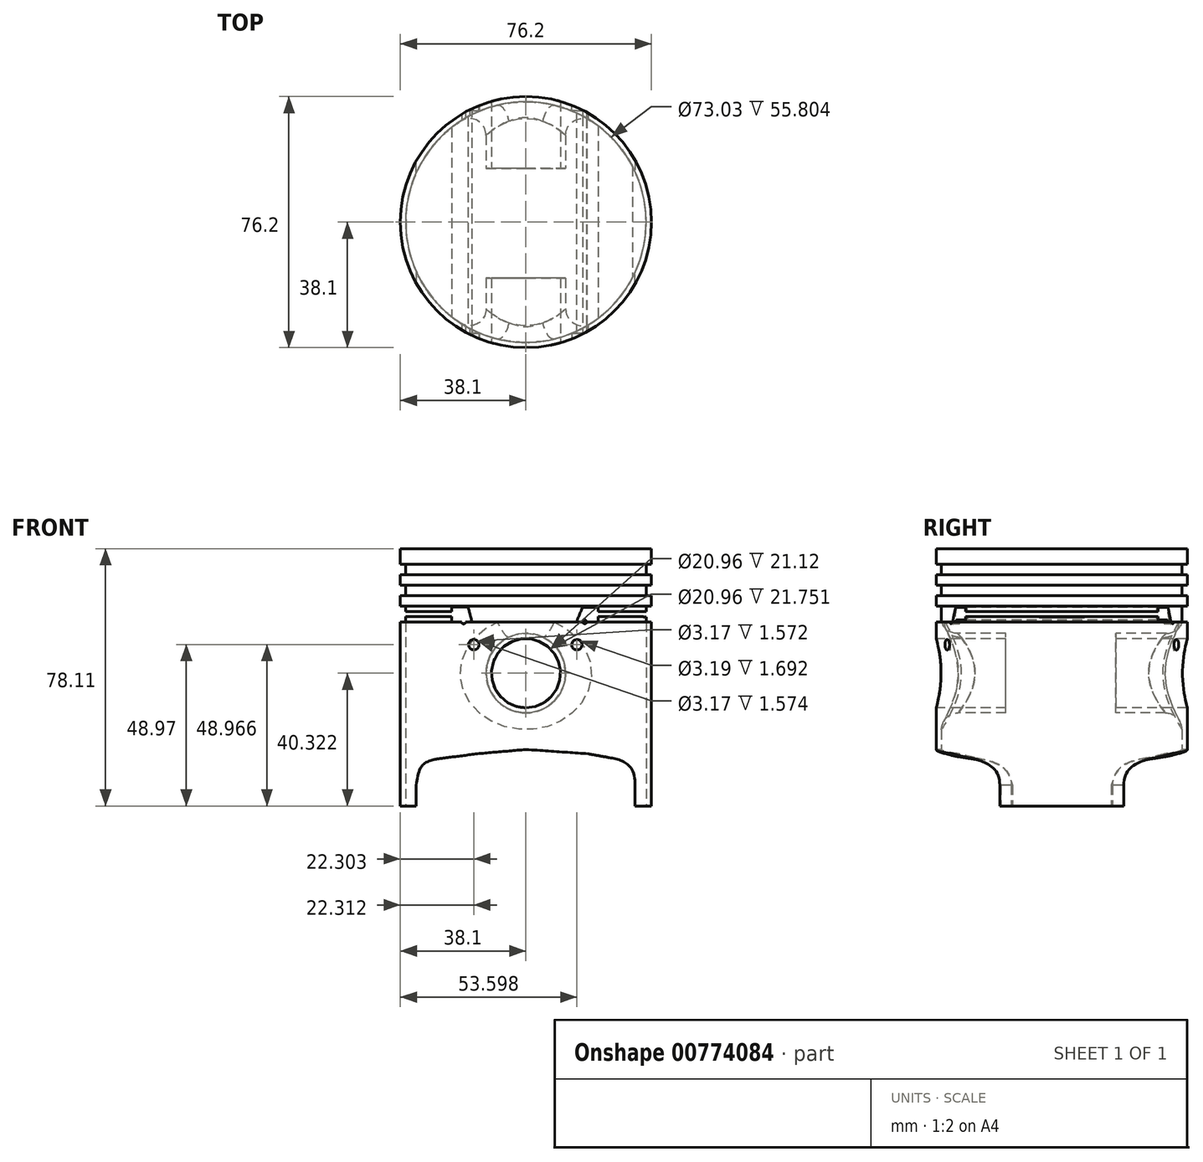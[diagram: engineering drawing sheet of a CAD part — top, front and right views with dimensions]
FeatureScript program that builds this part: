
annotation { "Feature Type Name" : "Feature", "Feature Type Description" : "" }
export const myFeature = defineFeature(function(context is Context, id is Id, definition is map)
    precondition{}
    {
        {
            var Q0;
            Q0=qCreatedBy(makeId("Top.planeOp"),FACE);
            var sketch = newSketch(context, id + "F0", { "sketchPlane" : qUnion([Q0])});
            skCircle(sketch, "E0", {"center": v(0, 0) * mm, "radius": 38.1 * mm});
            skSolve(sketch);
        }
        {
            var Q0;
            Q0=makeQuery(id+"F0.imprint","IMPRINT",FACE,{"disambiguationData":[TD([[makeQuery(id+"F0.imprint","IMPRINT",EDGE,{"derivedFrom":sQuery(id+"F0.wireOp",EDGE,"E0")}),1.0]])]});
            extrude(context, id + "F1", {"entities" : qUnion([Q0]), "depth" : 76.2 * mm, "offsetDistance" : 25.4 * mm});
        }
        {
            var Q0;
            Q0=qCreatedBy(makeId("Front.planeOp"),FACE);
            var sketch = newSketch(context, id + "F2", { "sketchPlane" : qUnion([Q0])});
            skCircle(sketch, "E1", {"center": v(0, 40.32) * mm, "radius": 10.48 * mm});
            skLineSegment(sketch, "E2", {"start": v(-33.3, 0) * mm, "end": v(-33.3, 6.35) * mm});
            skFitSpline(sketch, "E3", {"points": [v(-33.3, 6.35) * mm, v(-31.23, 12.52) * mm, v(-25.36, 14.53) * mm, v(-14.25, 15.88) * mm], "startDerivative": vector(3.82, 23.7) * mm, "endDerivative": vector(29.34, 3.33) * mm});
            skLineSegment(sketch, "E4", {"start": v(0.15, 29.85) * mm, "end": v(0.09, 17.15) * mm});
            skLineSegment(sketch, "E5", {"start": v(-14.25, 15.88) * mm, "end": v(0.09, 17.15) * mm});
            skLineSegment(sketch, "E6", {"start": v(33.13, 0) * mm, "end": v(33.13, 6.35) * mm});
            skLineSegment(sketch, "E7", {"start": v(0.09, 17.15) * mm, "end": v(18.85, 15.87) * mm});
            skPoint(sketch, "E8.2.internal.snap0", {"position": v(25.18, 5.16) * mm});
            skFitSpline(sketch, "E8", {"points": [v(18.85, 15.88) * mm, v(25.18, 14.52) * mm, v(25.18, 14.55) * mm], "startDerivative": vector(9.4, -2.2) * mm, "endDerivative": vector(-0.36, 0.95) * mm});
            skFitSpline(sketch, "E9", {"points": [v(25.18, 14.53) * mm, v(31.08, 12.52) * mm, v(33.13, 6.35) * mm], "startDerivative": vector(17.9, -3.2) * mm, "endDerivative": vector(-0.8, -16.63) * mm});
            skLineSegment(sketch, "E10", {"start": v(33.13, 0) * mm, "end": v(33.13, -4.57) * mm});
            skLineSegment(sketch, "E11", {"start": v(-33.3, 0) * mm, "end": v(-33.3, -6.09) * mm});
            skSolve(sketch);
        }
        {
            var Q0;
            Q0 = qSketchRegion(id + "F2", true);
            extrude(context, id + "F3", {"entities" : qUnion([Q0]), "operationType" : NewBodyOperationType.REMOVE, "oppositeDirection" : true, "depth" : 101.6 * mm, "offsetDistance" : 25.4 * mm, "hasSecondDirection" : true, "secondDirectionOppositeDirection" : false, "secondDirectionDepth" : 101.6 * mm});
        }
        {
            var Q0;
            Q0=qCreatedBy(makeId("Front.planeOp"),FACE);
            var sketch = newSketch(context, id + "F4", { "sketchPlane" : qUnion([Q0])});
            skLineSegment(sketch, "E12", {"start": v(33.14, -4.56) * mm, "end": v(33.14, 6.35) * mm});
            skFitSpline(sketch, "E13", {"points": [v(33.14, 6.35) * mm, v(32.85, 9.25) * mm, v(31.86, 11.6) * mm, v(30.17, 13.16) * mm, v(27.81, 14.2) * mm, v(25.2, 14.7) * mm, v(25.16, 14.64) * mm], "startDerivative": vector(-0.6, 14.42) * mm, "endDerivative": vector(43.72, -13.84) * mm});
            skLineSegment(sketch, "E14", {"start": v(0, 17.15) * mm, "end": v(18.85, 15.85) * mm});
            skLineSegment(sketch, "E15", {"start": v(18.85, 15.85) * mm, "end": v(25.2, 14.7) * mm});
            skLineSegment(sketch, "E16", {"start": v(-33.3, -6.02) * mm, "end": v(-33.3, 6.35) * mm});
            skFitSpline(sketch, "E17", {"points": [v(-33.3, 6.35) * mm, v(-32.71, 9.52) * mm, v(-31.31, 12.43) * mm, v(-28.65, 13.9) * mm, v(-25.45, 14.48) * mm], "startDerivative": vector(1.77, 12.54) * mm, "endDerivative": vector(12.84, 1.63) * mm});
            skLineSegment(sketch, "E18", {"start": v(-25.45, 14.48) * mm, "end": v(-14.19, 15.92) * mm});
            skLineSegment(sketch, "E19", {"start": v(-14.19, 15.92) * mm, "end": v(0, 17.15) * mm});
            skLineSegment(sketch, "E20", {"start": v(33.14, -4.56) * mm, "end": v(-33.3, -6.02) * mm});
            skSolve(sketch);
        }
        {
            var Q0;
            {var subQ2=sQuery(id+"F4.wireOp",EDGE,"E12");Q0=makeQuery(id+"F4.imprint","IMPRINT",FACE,{"disambiguationData":[TD([[makeQuery(id+"F4.imprint","IMPRINT",EDGE,{"derivedFrom":subQ2}),1.0]])]});}
            extrude(context, id + "F5", {"entities" : qUnion([Q0]), "operationType" : NewBodyOperationType.REMOVE, "oppositeDirection" : true, "depth" : 50.8 * mm, "offsetDistance" : 25.4 * mm, "hasSecondDirection" : true, "secondDirectionOppositeDirection" : false, "secondDirectionDepth" : 50.8 * mm});
        }
        {
            var Q0;
            Q0=makeQuery(id+"F5.boolean.opBoolean","COPY",FACE,{"derivedFrom":makeQuery(id+"F5.opExtrude","SWEPT_FACE",FACE,{"disambiguationData":[OSD([sQuery(id+"F4.wireOp",EDGE,"E19")])]})});
            var Q1;
            Q1=makeQuery(id+"F5.boolean.opBoolean","COPY",FACE,{"derivedFrom":makeQuery(id+"F5.opExtrude","SWEPT_FACE",FACE,{"disambiguationData":[OSD([sQuery(id+"F4.wireOp",EDGE,"E18")])]})});
            var Q2;
            Q2=makeQuery(id+"F5.boolean.opBoolean","COPY",FACE,{"derivedFrom":makeQuery(id+"F5.opExtrude","SWEPT_FACE",FACE,{"disambiguationData":[OSD([sQuery(id+"F4.wireOp",EDGE,"E17")])]})});
            var Q3;
            Q3=makeQuery(id+"F5.boolean.opBoolean","COPY",FACE,{"derivedFrom":makeQuery(id+"F5.opExtrude","SWEPT_FACE",FACE,{"disambiguationData":[OSD([sQuery(id+"F4.wireOp",EDGE,"E14")])]})});
            var Q4;
            Q4=makeQuery(id+"F5.boolean.opBoolean","COPY",FACE,{"derivedFrom":makeQuery(id+"F5.opExtrude","SWEPT_FACE",FACE,{"disambiguationData":[OSD([sQuery(id+"F4.wireOp",EDGE,"E15")])]})});
            var Q5;
            Q5=makeQuery(id+"F5.boolean.opBoolean","COPY",FACE,{"derivedFrom":makeQuery(id+"F5.opExtrude","SWEPT_FACE",FACE,{"disambiguationData":[OSD([sQuery(id+"F4.wireOp",EDGE,"E13")])]})});
            var Q6;
            {var subQ0=sQuery(id+"F0.wireOp",EDGE,"E0");Q6=makeQuery(id+"F5.boolean.opBoolean","SPLIT",FACE,{"disambiguationData":[TD([makeQuery(id+"F5.opExtrude","SWEPT_FACE",FACE,{"disambiguationData":[OSD([sQuery(id+"F4.wireOp",EDGE,"E12")])]})])],"derivedFrom":makeQuery(id+"F1.opExtrude","CAP_FACE",FACE,{"disambiguationData":[OSD([subQ0])],"isStart":true})});}
            var Q7;
            {var subQ0=sQuery(id+"F0.wireOp",EDGE,"E0");Q7=makeQuery(id+"F5.boolean.opBoolean","SPLIT",FACE,{"disambiguationData":[TD([makeQuery(id+"F5.opExtrude","SWEPT_FACE",FACE,{"disambiguationData":[OSD([sQuery(id+"F4.wireOp",EDGE,"E16")])]})])],"derivedFrom":makeQuery(id+"F1.opExtrude","CAP_FACE",FACE,{"disambiguationData":[OSD([subQ0])],"isStart":true})});}
            var Q8;
            Q8=makeQuery(id+"F5.boolean.opBoolean","COPY",FACE,{"derivedFrom":makeQuery(id+"F5.opExtrude","SWEPT_FACE",FACE,{"disambiguationData":[OSD([sQuery(id+"F4.wireOp",EDGE,"E16")])]})});
            var Q9;
            Q9=makeQuery(id+"F5.boolean.opBoolean","COPY",FACE,{"derivedFrom":makeQuery(id+"F5.opExtrude","SWEPT_FACE",FACE,{"disambiguationData":[OSD([sQuery(id+"F4.wireOp",EDGE,"E12")])]})});
            shell(context, id + "F6", {"entities" : qUnion([Q0, Q1, Q2, Q3, Q4, Q5, Q6, Q7, Q8, Q9]), "thickness" : 1.59 * mm});
        }
        {
            var Q0;
            Q0=qCreatedBy(makeId("Top.planeOp"),FACE);
            var sketch = newSketch(context, id + "F7", { "sketchPlane" : qUnion([Q0])});
            skLineSegment(sketch, "E21", {"start": v(-14.71, -16.98) * mm, "end": v(14.08, -16.98) * mm});
            skLineSegment(sketch, "E22", {"start": v(14.08, -16.98) * mm, "end": v(14.08, 16.35) * mm});
            skLineSegment(sketch, "E23", {"start": v(14.08, 16.35) * mm, "end": v(-13.8, 16.35) * mm});
            skLineSegment(sketch, "E24", {"start": v(-14.71, -16.98) * mm, "end": v(-13.8, 16.35) * mm});
            skLineSegment(sketch, "E25", {"start": v(0, -37.71) * mm, "end": v(-4.68, -37.71) * mm});
            skLineSegment(sketch, "E26", {"start": v(0, 37.07) * mm, "end": v(2.12, 37.07) * mm});
            skSolve(sketch);
        }
        {
            var Q0;
            Q0=makeQuery(id+"F7.imprint","IMPRINT",FACE,{"disambiguationData":[TD([[makeQuery(id+"F7.imprint","IMPRINT",EDGE,{"derivedFrom":sQuery(id+"F7.wireOp",EDGE,"E21")}),1.0]])]});
            extrude(context, id + "F8", {"entities" : qUnion([Q0]), "operationType" : NewBodyOperationType.REMOVE, "oppositeDirection" : true, "depth" : 25.4 * mm, "offsetDistance" : 25.4 * mm, "hasSecondDirection" : true, "secondDirectionOppositeDirection" : false, "secondDirectionDepth" : 55.88 * mm});
        }
        {
            var Q0;
            Q0=qCreatedBy(makeId("Front.planeOp"),FACE);
            var sketch = newSketch(context, id + "F9", { "sketchPlane" : qUnion([Q0])});
            skLineSegment(sketch, "E27", {"start": v(-50.34, 76.44) * mm, "end": v(-50.34, 55.8) * mm});
            skLineSegment(sketch, "E28", {"start": v(-50.34, 76.44) * mm, "end": v(56.34, 76.44) * mm});
            skLineSegment(sketch, "E29", {"start": v(56.34, 76.44) * mm, "end": v(56.34, 55.8) * mm});
            skLineSegment(sketch, "E30", {"start": v(56.34, 55.8) * mm, "end": v(-50.34, 55.8) * mm});
            skSolve(sketch);
        }
        {
            var Q0;
            Q0=makeQuery(id+"F9.imprint","IMPRINT",FACE,{"disambiguationData":[TD([[makeQuery(id+"F9.imprint","IMPRINT",EDGE,{"derivedFrom":sQuery(id+"F9.wireOp",EDGE,"E27")}),1.0]])]});
            extrude(context, id + "F10", {"entities" : qUnion([Q0]), "operationType" : NewBodyOperationType.REMOVE, "oppositeDirection" : true, "depth" : 81.28 * mm, "offsetDistance" : 25.4 * mm, "hasSecondDirection" : true, "secondDirectionOppositeDirection" : false, "secondDirectionDepth" : 50.8 * mm});
        }
        {
            var Q0;
            Q0=qCreatedBy(makeId("Top.planeOp"),FACE);
            cPlane(context, id + "F11", {"entities" : qUnion([Q0]), "cplaneType" : CPlaneType.OFFSET, "offset" : 55.88 * mm, "width" : 152.4 * mm, "height" : 152.4 * mm});
        }
        {
            var Q0;
            Q0=qCreatedBy(id+"F11.planeOp",FACE);
            var sketch = newSketch(context, id + "F12", { "sketchPlane" : qUnion([Q0])});
            skCircle(sketch, "E31", {"center": v(0, 0) * mm, "radius": 36.51 * mm});
            skSolve(sketch);
        }
        {
            var Q0;
            Q0 = qSketchRegion(id + "F12", true);
            extrude(context, id + "F13", {"entities" : qUnion([Q0]), "depth" : 4.76 * mm, "offsetDistance" : 25.4 * mm});
        }
        {
            var Q0;
            Q0=qCreatedBy(id+"F11.planeOp",FACE);
            cPlane(context, id + "F14", {"entities" : qUnion([Q0]), "cplaneType" : CPlaneType.OFFSET, "offset" : 4.76 * mm, "width" : 152.4 * mm, "height" : 152.4 * mm});
        }
        {
            var Q0;
            Q0=qCreatedBy(id+"F14.planeOp",FACE);
            var sketch = newSketch(context, id + "F15", { "sketchPlane" : qUnion([Q0])});
            skCircle(sketch, "E32", {"center": v(0, 0) * mm, "radius": 38.1 * mm});
            skSolve(sketch);
        }
        {
            var Q0;
            Q0 = qSketchRegion(id + "F15", true);
            extrude(context, id + "F16", {"entities" : qUnion([Q0]), "operationType" : NewBodyOperationType.ADD, "depth" : 3.17 * mm, "offsetDistance" : 25.4 * mm});
        }
        {
            var Q0;
            Q0=qCreatedBy(id+"F14.planeOp",FACE);
            cPlane(context, id + "F17", {"entities" : qUnion([Q0]), "cplaneType" : CPlaneType.OFFSET, "offset" : 3.17 * mm, "width" : 152.4 * mm, "height" : 152.4 * mm});
        }
        {
            var Q0;
            Q0=qCreatedBy(id+"F17.planeOp",FACE);
            var sketch = newSketch(context, id + "F18", { "sketchPlane" : qUnion([Q0])});
            skCircle(sketch, "E33", {"center": v(0, 0) * mm, "radius": 36.51 * mm});
            skSolve(sketch);
        }
        {
            var Q0;
            Q0 = qSketchRegion(id + "F18", true);
            extrude(context, id + "F19", {"entities" : qUnion([Q0]), "operationType" : NewBodyOperationType.ADD, "depth" : 3.17 * mm, "offsetDistance" : 25.4 * mm});
        }
        {
            var Q0;
            Q0=qCreatedBy(id+"F17.planeOp",FACE);
            cPlane(context, id + "F20", {"entities" : qUnion([Q0]), "cplaneType" : CPlaneType.OFFSET, "offset" : 3.17 * mm, "width" : 152.4 * mm, "height" : 152.4 * mm});
        }
        {
            var Q0;
            Q0=qCreatedBy(id+"F20.planeOp",FACE);
            var sketch = newSketch(context, id + "F21", { "sketchPlane" : qUnion([Q0])});
            skCircle(sketch, "E34", {"center": v(0, 0) * mm, "radius": 38.1 * mm});
            skSolve(sketch);
        }
        {
            var Q0;
            Q0 = qSketchRegion(id + "F21", true);
            extrude(context, id + "F22", {"entities" : qUnion([Q0]), "operationType" : NewBodyOperationType.ADD, "depth" : 3.17 * mm, "offsetDistance" : 25.4 * mm});
        }
        {
            var Q0;
            Q0=qCreatedBy(id+"F20.planeOp",FACE);
            cPlane(context, id + "F23", {"entities" : qUnion([Q0]), "cplaneType" : CPlaneType.OFFSET, "offset" : 3.17 * mm, "width" : 152.4 * mm, "height" : 152.4 * mm});
        }
        {
            var Q0;
            Q0=qCreatedBy(id+"F23.planeOp",FACE);
            var sketch = newSketch(context, id + "F24", { "sketchPlane" : qUnion([Q0])});
            skCircle(sketch, "E35", {"center": v(0, 0) * mm, "radius": 36.51 * mm});
            skSolve(sketch);
        }
        {
            var Q0;
            Q0 = qSketchRegion(id + "F24", true);
            extrude(context, id + "F25", {"entities" : qUnion([Q0]), "operationType" : NewBodyOperationType.ADD, "depth" : 3.17 * mm, "offsetDistance" : 25.4 * mm});
        }
        {
            var Q0;
            Q0=qCreatedBy(id+"F23.planeOp",FACE);
            cPlane(context, id + "F26", {"entities" : qUnion([Q0]), "cplaneType" : CPlaneType.OFFSET, "offset" : 3.17 * mm, "width" : 152.4 * mm, "height" : 152.4 * mm});
        }
        {
            var Q0;
            Q0=qCreatedBy(id+"F26.planeOp",FACE);
            var sketch = newSketch(context, id + "F27", { "sketchPlane" : qUnion([Q0])});
            skCircle(sketch, "E36", {"center": v(0, 0) * mm, "radius": 38.1 * mm});
            skSolve(sketch);
        }
        {
            var Q0;
            Q0 = qSketchRegion(id + "F27", true);
            extrude(context, id + "F28", {"entities" : qUnion([Q0]), "operationType" : NewBodyOperationType.ADD, "depth" : 4.76 * mm, "offsetDistance" : 25.4 * mm});
        }
        {
            var Q0;
            Q0=qCreatedBy(makeId("Front.planeOp"),FACE);
            cPlane(context, id + "F29", {"entities" : qUnion([Q0]), "cplaneType" : CPlaneType.OFFSET, "offset" : 39.37 * mm, "width" : 152.4 * mm, "height" : 152.4 * mm});
        }
        {
            var Q0;
            Q0=qCreatedBy(id+"F29.planeOp",FACE);
            var sketch = newSketch(context, id + "F30", { "sketchPlane" : qUnion([Q0])});
            skLineSegment(sketch, "E37", {"start": v(0, 29.9) * mm, "end": v(18.92, 29.9) * mm});
            skLineSegment(sketch, "E38", {"start": v(0, 29.9) * mm, "end": v(-18.94, 29.9) * mm});
            skLineSegment(sketch, "E39", {"start": v(18.92, 29.9) * mm, "end": v(10.3, 39.61) * mm});
            skLineSegment(sketch, "E40", {"start": v(-18.94, 29.9) * mm, "end": v(-10.45, 39.48) * mm});
            skLineSegment(sketch, "E41", {"start": v(10.3, 39.61) * mm, "end": v(-10.45, 39.48) * mm});
            skLineSegment(sketch, "E42", {"start": v(18.92, 29.9) * mm, "end": v(18.92, 48.96) * mm});
            skLineSegment(sketch, "E43", {"start": v(-18.94, 29.9) * mm, "end": v(-18.94, 48.96) * mm});
            skLineSegment(sketch, "E44", {"start": v(-6.27, 48.96) * mm, "end": v(-15.8, 48.96) * mm});
            skLineSegment(sketch, "E45", {"start": v(5.97, 48.96) * mm, "end": v(15.5, 48.96) * mm});
            skCircle(sketch, "E46", {"center": v(-15.8, 48.96) * mm, "radius": 1.59 * mm});
            skCircle(sketch, "E47", {"center": v(15.5, 48.96) * mm, "radius": 1.59 * mm});
            skSolve(sketch);
        }
        {
            var Q0;
            Q0=makeQuery(id+"F30.imprint","IMPRINT",FACE,{"disambiguationData":[TD([[makeQuery(id+"F30.imprint","IMPRINT",EDGE,{"derivedFrom":sQuery(id+"F30.wireOp",EDGE,"E47")}),1.0]])]});
            extrude(context, id + "F31", {"entities" : qUnion([Q0]), "operationType" : NewBodyOperationType.REMOVE, "oppositeDirection" : true, "depth" : 5.6 * mm, "offsetDistance" : 25.4 * mm});
        }
        {
            var Q0;
            Q0=makeQuery(id+"F30.imprint","IMPRINT",FACE,{"disambiguationData":[TD([[makeQuery(id+"F30.imprint","IMPRINT",EDGE,{"derivedFrom":sQuery(id+"F30.wireOp",EDGE,"E46")}),1.0]])]});
            extrude(context, id + "F32", {"entities" : qUnion([Q0]), "operationType" : NewBodyOperationType.REMOVE, "oppositeDirection" : true, "depth" : 5.6 * mm, "offsetDistance" : 25.4 * mm});
        }
        {
            var Q0;
            Q0=qCreatedBy(makeId("Front.planeOp"),FACE);
            cPlane(context, id + "F33", {"entities" : qUnion([Q0]), "cplaneType" : CPlaneType.OFFSET, "offset" : 39.37 * mm, "oppositeDirection" : true, "width" : 152.4 * mm, "height" : 152.4 * mm});
        }
        {
            var Q0;
            Q0=qCreatedBy(id+"F33.planeOp",FACE);
            var sketch = newSketch(context, id + "F34", { "sketchPlane" : qUnion([Q0])});
            skLineSegment(sketch, "E48", {"start": v(-18.94, 48.97) * mm, "end": v(-15.79, 48.97) * mm});
            skLineSegment(sketch, "E49", {"start": v(18.92, 48.97) * mm, "end": v(15.5, 48.97) * mm});
            skCircle(sketch, "E50", {"center": v(-15.79, 48.97) * mm, "radius": 1.58 * mm});
            skCircle(sketch, "E51", {"center": v(15.5, 48.97) * mm, "radius": 1.6 * mm});
            skSolve(sketch);
        }
        {
            var Q0;
            Q0=makeQuery(id+"F34.imprint","IMPRINT",FACE,{"disambiguationData":[TD([[makeQuery(id+"F34.imprint","IMPRINT",EDGE,{"derivedFrom":sQuery(id+"F34.wireOp",EDGE,"E51")}),1.0]])]});
            extrude(context, id + "F35", {"entities" : qUnion([Q0]), "operationType" : NewBodyOperationType.REMOVE, "depth" : 5.6 * mm, "offsetDistance" : 25.4 * mm});
        }
        {
            var Q0;
            Q0=makeQuery(id+"F34.imprint","IMPRINT",FACE,{"disambiguationData":[TD([[makeQuery(id+"F34.imprint","IMPRINT",EDGE,{"derivedFrom":sQuery(id+"F34.wireOp",EDGE,"E50")}),1.0]])]});
            extrude(context, id + "F36", {"entities" : qUnion([Q0]), "operationType" : NewBodyOperationType.REMOVE, "depth" : 5.6 * mm, "offsetDistance" : 25.4 * mm});
        }
        {
            var Q0;
            {var subQ0=sQuery(id+"F2.wireOp",EDGE,"E1");var subQ1=sQuery(id+"F0.wireOp",EDGE,"E0");Q0=makeQuery(id+"F6.opShell","OFFSET_EDGE",EDGE,{"disambiguationData":[OSD([subQ1,subQ0]),TDD([makeQuery(id+"F3.boolean.opBoolean","INTERSECT",EDGE,{"disambiguationData":[OD(1.0)],"derivedFrom":[makeQuery(id+"F1.opExtrude","SWEPT_FACE",FACE,{"disambiguationData":[OSD([subQ1])]}),makeQuery(id+"F3.opExtrude","SWEPT_FACE",FACE,{"disambiguationData":[OSD([subQ0])]})]})])]});}
            var Q1;
            {var subQ0=sQuery(id+"F2.wireOp",EDGE,"E1");var subQ1=sQuery(id+"F0.wireOp",EDGE,"E0");Q1=makeQuery(id+"F6.opShell","OFFSET_EDGE",EDGE,{"disambiguationData":[OSD([subQ1,subQ0]),TDD([makeQuery(id+"F3.boolean.opBoolean","INTERSECT",EDGE,{"disambiguationData":[OD(0.0)],"derivedFrom":[makeQuery(id+"F1.opExtrude","SWEPT_FACE",FACE,{"disambiguationData":[OSD([subQ1])]}),makeQuery(id+"F3.opExtrude","SWEPT_FACE",FACE,{"disambiguationData":[OSD([subQ0])]})]})])]});}
            fillet(context, id + "F37", {"entities" : qUnion([Q0, Q1]), "radius" : 5.08 * mm, "tangentPropagation" : true, "allowEdgeOverflow" : false});
        }
        {
            var Q0;
            Q0=qCreatedBy(makeId("Front.planeOp"),FACE);
            cPlane(context, id + "F38", {"entities" : qUnion([Q0]), "cplaneType" : CPlaneType.OFFSET, "offset" : 35.56 * mm, "width" : 152.4 * mm, "height" : 152.4 * mm});
        }
        {
            var Q0;
            Q0=qCreatedBy(id+"F38.planeOp",FACE);
            var sketch = newSketch(context, id + "F39", { "sketchPlane" : qUnion([Q0])});
            skLineSegment(sketch, "E52", {"start": v(-24.7, 60.59) * mm, "end": v(-24.7, 59) * mm});
            skLineSegment(sketch, "E53", {"start": v(-24.7, 55.84) * mm, "end": v(-24.7, 57.43) * mm});
            skLineSegment(sketch, "E54", {"start": v(-16.33, 55.8) * mm, "end": v(-17.53, 60.46) * mm});
            skLineSegment(sketch, "E55", {"start": v(-17.53, 60.46) * mm, "end": v(-22.53, 60.46) * mm});
            skLineSegment(sketch, "E56", {"start": v(-24.7, 59) * mm, "end": v(-22.55, 59) * mm});
            skLineSegment(sketch, "E57", {"start": v(-22.53, 60.46) * mm, "end": v(-22.55, 59) * mm});
            skLineSegment(sketch, "E58", {"start": v(-24.7, 59) * mm, "end": v(-37.57, 59) * mm});
            skLineSegment(sketch, "E59", {"start": v(-22.55, 55.84) * mm, "end": v(-22.55, 57.44) * mm});
            skLineSegment(sketch, "E60", {"start": v(-22.55, 57.44) * mm, "end": v(-37.66, 57.43) * mm});
            skLineSegment(sketch, "E61", {"start": v(-37.57, 59) * mm, "end": v(-37.66, 57.43) * mm});
            skLineSegment(sketch, "E62", {"start": v(-22.55, 55.84) * mm, "end": v(-20.37, 55.84) * mm});
            skLineSegment(sketch, "E63", {"start": v(-20.37, 55.84) * mm, "end": v(-18.9, 55.84) * mm});
            skLineSegment(sketch, "E64", {"start": v(-18.9, 55.84) * mm, "end": v(-16.33, 55.8) * mm});
            skCircle(sketch, "E65", {"center": v(-18.9, 55.84) * mm, "radius": 0.58 * mm});
            skLineSegment(sketch, "E66", {"start": v(32.4, 55.86) * mm, "end": v(32.4, 57.46) * mm});
            skLineSegment(sketch, "E67", {"start": v(32.33, 60.55) * mm, "end": v(32.33, 58.95) * mm});
            skLineSegment(sketch, "E68", {"start": v(17.18, 49.04) * mm, "end": v(17.18, 60.33) * mm});
            skLineSegment(sketch, "E69", {"start": v(17.18, 60.33) * mm, "end": v(15.37, 55.9) * mm});
            skLineSegment(sketch, "E70", {"start": v(17.18, 60.33) * mm, "end": v(21.95, 60.33) * mm});
            skLineSegment(sketch, "E71", {"start": v(32.33, 58.95) * mm, "end": v(21.95, 58.95) * mm});
            skLineSegment(sketch, "E72", {"start": v(21.95, 58.95) * mm, "end": v(21.95, 60.33) * mm});
            skLineSegment(sketch, "E73", {"start": v(32.4, 57.46) * mm, "end": v(21.95, 57.46) * mm});
            skLineSegment(sketch, "E74", {"start": v(21.95, 57.46) * mm, "end": v(21.95, 55.9) * mm});
            skLineSegment(sketch, "E75", {"start": v(21.95, 55.9) * mm, "end": v(15.37, 55.9) * mm});
            skLineSegment(sketch, "E76", {"start": v(17.86, 55.9) * mm, "end": v(15.37, 55.9) * mm});
            skCircle(sketch, "E77", {"center": v(17.86, 55.9) * mm, "radius": 0.58 * mm});
            skLineSegment(sketch, "E78", {"start": v(32.33, 58.95) * mm, "end": v(37.97, 58.95) * mm});
            skLineSegment(sketch, "E79", {"start": v(37.97, 58.95) * mm, "end": v(37.97, 57.4) * mm});
            skLineSegment(sketch, "E80", {"start": v(37.97, 57.4) * mm, "end": v(32.4, 57.46) * mm});
            skSolve(sketch);
        }
        {
            var Q0;
            {var subQ4=sQuery(id+"F39.wireOp",EDGE,"E54");Q0=makeQuery(id+"F39.imprint","IMPRINT",FACE,{"disambiguationData":[TD([[makeQuery(id+"F39.imprint","IMPRINT",EDGE,{"derivedFrom":subQ4}),1.0]])]});}
            var Q1;
            {var subQ8=sQuery(id+"F39.wireOp",EDGE,"E70");Q1=makeQuery(id+"F39.imprint","IMPRINT",FACE,{"disambiguationData":[TD([[makeQuery(id+"F39.imprint","IMPRINT",EDGE,{"derivedFrom":subQ8}),-1.0]])]});}
            var Q2;
            {var subQ0=sQuery(id+"F39.wireOp",EDGE,"E69");Q2=makeQuery(id+"F39.imprint","IMPRINT",FACE,{"disambiguationData":[TD([[makeQuery(id+"F39.imprint","IMPRINT",EDGE,{"derivedFrom":subQ0}),1.0]])]});}
            var Q3;
            {var subQ0=sQuery(id+"F39.wireOp",EDGE,"E76");var subQ1=sQuery(id+"F39.wireOp",EDGE,"E75");var subQ2=makeQuery(id+"F39.imprint","INTERSECT",VERTEX,{"derivedFrom":[subQ1,subQ0]});Q3=makeQuery(id+"F39.imprint","IMPRINT",FACE,{"disambiguationData":[TD([[makeQuery(id+"F39.imprint","IMPRINT",EDGE,{"disambiguationData":[TD([[subQ2,1.0]])],"derivedFrom":subQ1}),1.0]])]});}
            var Q4;
            {var subQ0=sQuery(id+"F39.wireOp",EDGE,"E64");var subQ1=sQuery(id+"F39.wireOp",EDGE,"E63");var subQ2=makeQuery(id+"F39.imprint","INTERSECT",VERTEX,{"derivedFrom":[subQ1,subQ0]});Q4=makeQuery(id+"F39.imprint","IMPRINT",FACE,{"disambiguationData":[TD([[makeQuery(id+"F39.imprint","IMPRINT",EDGE,{"disambiguationData":[TD([[subQ2,1.0]])],"derivedFrom":subQ1}),-1.0]])]});}
            var Q5;
            {var subQ0=sQuery(id+"F39.wireOp",EDGE,"E64");var subQ1=sQuery(id+"F39.wireOp",EDGE,"E63");var subQ2=makeQuery(id+"F39.imprint","INTERSECT",VERTEX,{"derivedFrom":[subQ1,subQ0]});Q5=makeQuery(id+"F39.imprint","IMPRINT",FACE,{"disambiguationData":[TD([[makeQuery(id+"F39.imprint","IMPRINT",EDGE,{"disambiguationData":[TD([[subQ2,1.0]])],"derivedFrom":subQ1}),1.0]])]});}
            var Q6;
            {var subQ0=sQuery(id+"F39.wireOp",EDGE,"E76");var subQ1=sQuery(id+"F39.wireOp",EDGE,"E75");var subQ2=makeQuery(id+"F39.imprint","INTERSECT",VERTEX,{"derivedFrom":[subQ1,subQ0]});Q6=makeQuery(id+"F39.imprint","IMPRINT",FACE,{"disambiguationData":[TD([[makeQuery(id+"F39.imprint","IMPRINT",EDGE,{"disambiguationData":[TD([[subQ2,1.0]])],"derivedFrom":subQ1}),-1.0]])]});}
            extrude(context, id + "F40", {"entities" : qUnion([Q0, Q1, Q2, Q3, Q4, Q5, Q6]), "operationType" : NewBodyOperationType.REMOVE, "oppositeDirection" : true, "depth" : 203.2 * mm, "offsetDistance" : 25.4 * mm, "hasSecondDirection" : true, "secondDirectionOppositeDirection" : false, "secondDirectionDepth" : 25.4 * mm});
        }
    });
